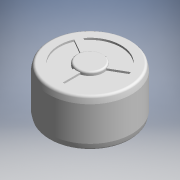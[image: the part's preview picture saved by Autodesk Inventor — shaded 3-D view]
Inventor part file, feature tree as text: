
AUTODESK INVENTOR PART (.ipt)
format: ipt  version: 2017.3 (Build 213256000, 256)  size: 169,984 bytes
history: native  units: mm (DEFAULTED — no unit token found)
features: other x7, sketch x2, revolve x1, extrude x1
ambient origin geometry x8: Origin, YZ Plane, XZ Plane, XY Plane, X Axis, Y Axis, Z Axis, Center Point
bodies: Solid1 (feature_tree)
feature tree (11):
  revolve  "Revolution1"  [1 undecoded]
  extrude  "Extrusion1"  [1 undecoded]
  other  "wheel_to_body_XY"
  other  "wheel_to_body_YZ"
  other  "wheel_to_body_ZX"
  other  "wheel_to_body_X"
  other  "wheel_to_body_Y"
  other  "wheel_to_body_Z"
  other  "wheel_to_body_Center"
  sketch  "Sketch_1"  dims[d0=360.0deg d1=28.0mm d2=0.0mm]
  sketch  "Sketch_5"
note: 2 required parameter values undecoded (feature->parameter linkage not recoverable at this tier; creation-order binding heuristic only, values carry confidence <= 0.55)